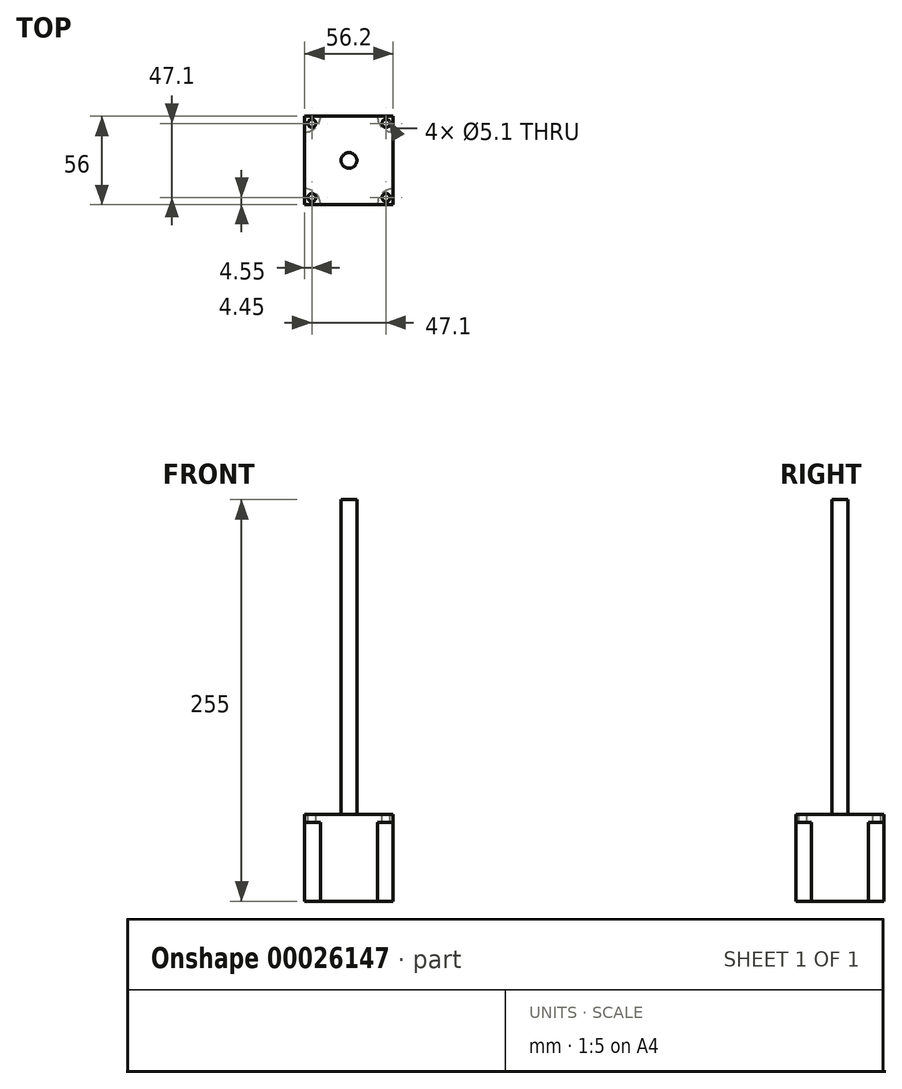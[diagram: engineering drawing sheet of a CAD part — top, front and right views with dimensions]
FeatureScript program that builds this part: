
annotation { "Feature Type Name" : "Feature", "Feature Type Description" : "" }
export const myFeature = defineFeature(function(context is Context, id is Id, definition is map)
    precondition{}
    {
        {
            var Q0;
            Q0=qCreatedBy(makeId("Front.planeOp"),FACE);
            var sketch = newSketch(context, id + "F0", { "sketchPlane" : qUnion([Q0])});
            skLineSegment(sketch, "E0.rect.bottom", {"start": v(28.1, -27.5) * mm, "end": v(-28.1, -27.5) * mm});
            skLineSegment(sketch, "E0.rect.top", {"start": v(28.1, 27.5) * mm, "end": v(-28.1, 27.5) * mm});
            skLineSegment(sketch, "E0.rect.left", {"start": v(28.1, -27.5) * mm, "end": v(28.1, 27.5) * mm});
            skLineSegment(sketch, "E0.rect.right", {"start": v(-28.1, -27.5) * mm, "end": v(-28.1, 27.5) * mm});
            skPoint(sketch, "E0.rect.middle", {"position": v(0, 0) * mm});
            skSolve(sketch);
        }
        {
            var Q0;
            Q0 = qSketchRegion(id + "F0", true);
            extrude(context, id + "F1", {"entities" : qUnion([Q0]), "endBound" : BoundingType.SYMMETRIC, "depth" : 56 * mm});
        }
        {
            var Q0;
            Q0=makeQuery(id+"F1.opExtrude","SWEPT_FACE",FACE,{"disambiguationData":[OSD([sQuery(id+"F0.wireOp",EDGE,"E0.rect.bottom")])]});
            var sketch = newSketch(context, id + "F2", { "sketchPlane" : qUnion([Q0])});
            skCircle(sketch, "E1", {"center": v(-28.1, 28) * mm, "radius": 10 * mm});
            skCircle(sketch, "E2", {"center": v(-28.1, -28) * mm, "radius": 10 * mm});
            skCircle(sketch, "E3", {"center": v(28.1, -28) * mm, "radius": 10 * mm});
            skCircle(sketch, "E4", {"center": v(28.1, 28) * mm, "radius": 10 * mm});
            skSolve(sketch);
        }
        {
            var Q0;
            {var subQ0=sQuery(id+"F0.wireOp",EDGE,"E0.rect.bottom");var subQ1=makeQuery(id+"F1.opExtrude","CAP_EDGE",EDGE,{"disambiguationData":[OSD([subQ0])],"isStart":false});var subQ2=sQuery(id+"F2.wireOp",EDGE,"E1");var subQ3=makeQuery(id+"F2.imprint","INTERSECT",VERTEX,{"derivedFrom":[subQ1,subQ2]});Q0=makeQuery(id+"F2.imprint","IMPRINT",FACE,{"disambiguationData":[TD([[makeQuery(id+"F2.imprint","IMPRINT",EDGE,{"disambiguationData":[TD([[subQ3,1.0]])],"derivedFrom":subQ2}),1.0]])]});}
            var Q1;
            {var subQ0=sQuery(id+"F0.wireOp",EDGE,"E0.rect.bottom");var subQ1=makeQuery(id+"F1.opExtrude","CAP_EDGE",EDGE,{"disambiguationData":[OSD([subQ0])],"isStart":true});var subQ2=sQuery(id+"F2.wireOp",EDGE,"E2");var subQ3=makeQuery(id+"F2.imprint","INTERSECT",VERTEX,{"derivedFrom":[subQ1,subQ2]});Q1=makeQuery(id+"F2.imprint","IMPRINT",FACE,{"disambiguationData":[TD([[makeQuery(id+"F2.imprint","IMPRINT",EDGE,{"disambiguationData":[TD([[subQ3,-1.0]])],"derivedFrom":subQ2}),1.0]])]});}
            var Q2;
            {var subQ0=sQuery(id+"F0.wireOp",EDGE,"E0.rect.bottom");var subQ1=makeQuery(id+"F1.opExtrude","CAP_EDGE",EDGE,{"disambiguationData":[OSD([subQ0])],"isStart":true});var subQ2=sQuery(id+"F2.wireOp",EDGE,"E3");var subQ3=makeQuery(id+"F2.imprint","INTERSECT",VERTEX,{"derivedFrom":[subQ1,subQ2]});Q2=makeQuery(id+"F2.imprint","IMPRINT",FACE,{"disambiguationData":[TD([[makeQuery(id+"F2.imprint","IMPRINT",EDGE,{"disambiguationData":[TD([[subQ3,1.0]])],"derivedFrom":subQ2}),1.0]])]});}
            var Q3;
            {var subQ0=sQuery(id+"F0.wireOp",EDGE,"E0.rect.bottom");var subQ1=makeQuery(id+"F1.opExtrude","CAP_EDGE",EDGE,{"disambiguationData":[OSD([subQ0])],"isStart":false});var subQ2=sQuery(id+"F2.wireOp",EDGE,"E4");var subQ3=makeQuery(id+"F2.imprint","INTERSECT",VERTEX,{"derivedFrom":[subQ1,subQ2]});Q3=makeQuery(id+"F2.imprint","IMPRINT",FACE,{"disambiguationData":[TD([[makeQuery(id+"F2.imprint","IMPRINT",EDGE,{"disambiguationData":[TD([[subQ3,-1.0]])],"derivedFrom":subQ2}),1.0]])]});}
            extrude(context, id + "F3", {"entities" : qUnion([Q0, Q1, Q2, Q3]), "operationType" : NewBodyOperationType.REMOVE, "oppositeDirection" : true, "depth" : 50 * mm});
        }
        {
            var Q0;
            Q0=makeQuery(id+"F1.opExtrude","SWEPT_FACE",FACE,{"disambiguationData":[OSD([sQuery(id+"F0.wireOp",EDGE,"E0.rect.top")])]});
            var sketch = newSketch(context, id + "F4", { "sketchPlane" : qUnion([Q0])});
            skCircle(sketch, "E5", {"center": v(0, 0) * mm, "radius": 5 * mm});
            skSolve(sketch);
        }
        {
            var Q0;
            Q0=makeQuery(id+"F4.imprint","IMPRINT",FACE,{"disambiguationData":[TD([[makeQuery(id+"F4.imprint","IMPRINT",EDGE,{"derivedFrom":sQuery(id+"F4.wireOp",EDGE,"E5")}),1.0]])]});
            extrude(context, id + "F5", {"entities" : qUnion([Q0]), "operationType" : NewBodyOperationType.ADD, "depth" : 200 * mm});
        }
        {
            var Q0;
            Q0=makeQuery(id+"F1.opExtrude","SWEPT_FACE",FACE,{"disambiguationData":[OSD([sQuery(id+"F0.wireOp",EDGE,"E0.rect.top")])]});
            var sketch = newSketch(context, id + "F6", { "sketchPlane" : qUnion([Q0])});
            skLineSegment(sketch, "E6.rect.bottom", {"start": v(23.55, 23.55) * mm, "end": v(-23.55, 23.55) * mm, "construction": true});
            skLineSegment(sketch, "E6.rect.top", {"start": v(23.55, -23.55) * mm, "end": v(-23.55, -23.55) * mm, "construction": true});
            skLineSegment(sketch, "E6.rect.left", {"start": v(23.55, 23.55) * mm, "end": v(23.55, -23.55) * mm, "construction": true});
            skLineSegment(sketch, "E6.rect.right", {"start": v(-23.55, 23.55) * mm, "end": v(-23.55, -23.55) * mm, "construction": true});
            skPoint(sketch, "E6.rect.middle", {"position": v(0, 0) * mm});
            skCircle(sketch, "E7", {"center": v(23.55, 23.55) * mm, "radius": 2.55 * mm});
            skCircle(sketch, "E8", {"center": v(23.55, -23.55) * mm, "radius": 2.55 * mm});
            skCircle(sketch, "E9", {"center": v(-23.55, -23.55) * mm, "radius": 2.55 * mm});
            skCircle(sketch, "E10", {"center": v(-23.55, 23.55) * mm, "radius": 2.55 * mm});
            skSolve(sketch);
        }
        {
            var Q0;
            Q0 = qSketchRegion(id + "F6", true);
            extrude(context, id + "F7", {"entities" : qUnion([Q0]), "operationType" : NewBodyOperationType.REMOVE, "endBound" : BoundingType.THROUGH_ALL, "oppositeDirection" : true, "depth" : 25 * mm});
        }
    });
